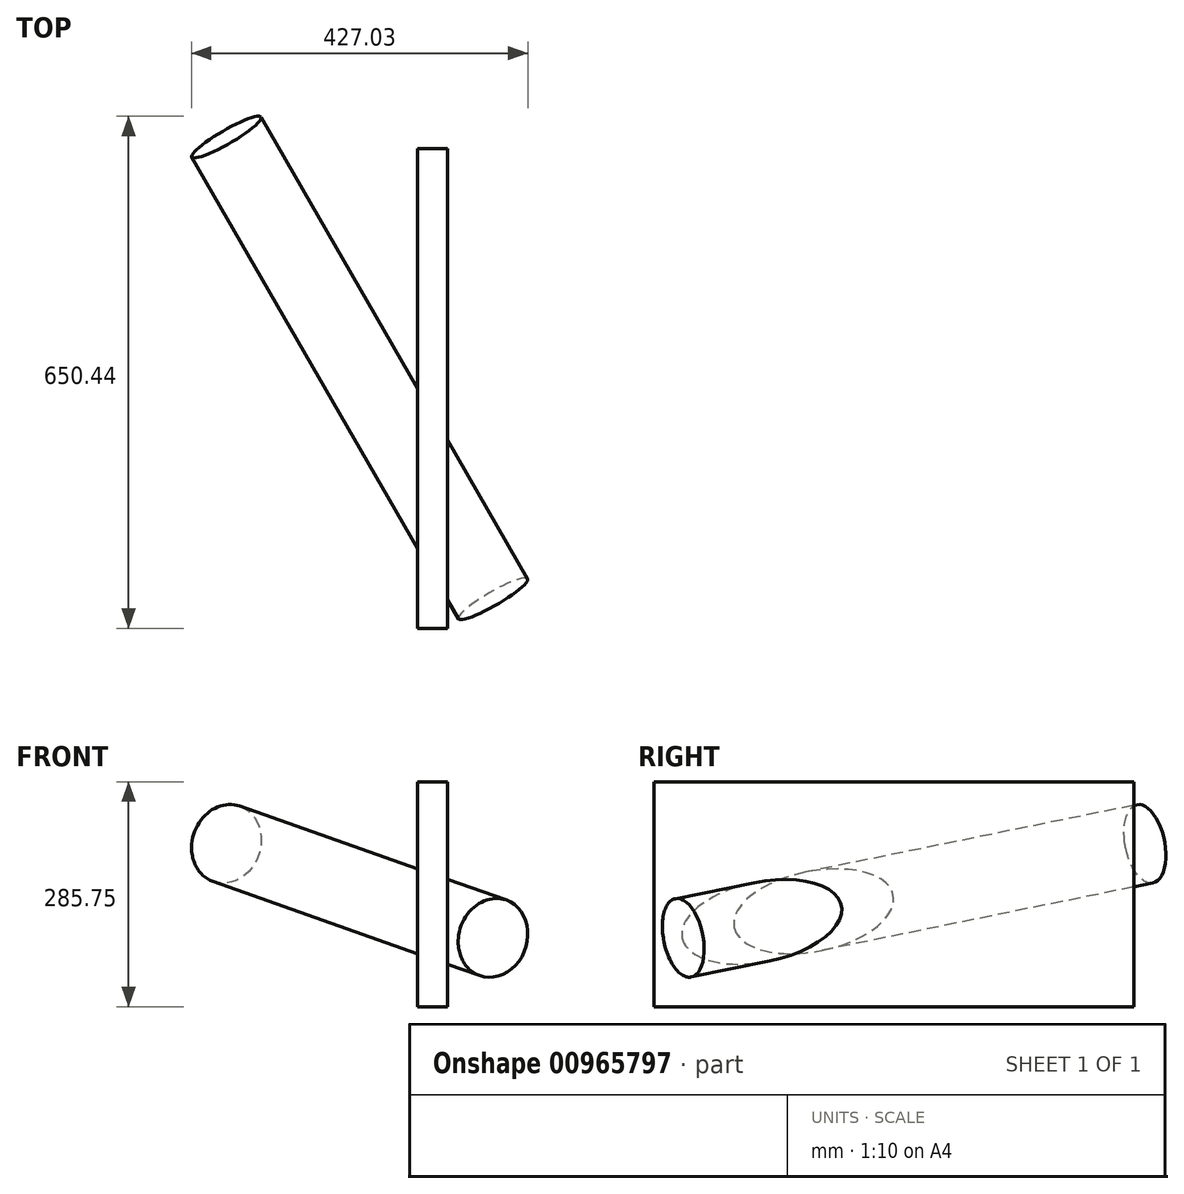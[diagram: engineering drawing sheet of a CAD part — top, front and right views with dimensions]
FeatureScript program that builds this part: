
annotation { "Feature Type Name" : "Feature", "Feature Type Description" : "" }
export const myFeature = defineFeature(function(context is Context, id is Id, definition is map)
    precondition{}
    {
        {
            var Q0;
            Q0=qCreatedBy(makeId("Front.planeOp"),FACE);
            var sketch = newSketch(context, id + "F0", { "sketchPlane" : qUnion([Q0])});
            skLineSegment(sketch, "E0.bottom", {"start": v(0, 0) * mm, "end": v(38.1, 0) * mm});
            skLineSegment(sketch, "E0.top", {"start": v(0, 285.75) * mm, "end": v(38.1, 285.75) * mm});
            skLineSegment(sketch, "E0.left", {"start": v(0, 0) * mm, "end": v(0, 285.75) * mm});
            skLineSegment(sketch, "E0.right", {"start": v(38.1, 0) * mm, "end": v(38.1, 285.75) * mm});
            skSolve(sketch);
        }
        {
            var Q0;
            Q0 = qSketchRegion(id + "F0", true);
            extrude(context, id + "F1", {"entities" : qUnion([Q0]), "oppositeDirection" : true, "depth" : 609.6 * mm, "offsetDistance" : 25.4 * mm});
        }
        {
            var Q0;
            Q0=makeQuery(id+"F1.opExtrude","CAP_EDGE",EDGE,{"disambiguationData":[OSD([sQuery(id+"F0.wireOp",EDGE,"E0.left")])],"isStart":true});
            cPlane(context, id + "F2", {"entities" : qUnion([Q0]), "cplaneType" : CPlaneType.LINE_ANGLE, "offset" : 25.4 * mm, "angle" : 60 * degree, "oppositeDirection" : true, "width" : 152.4 * mm, "height" : 152.4 * mm});
        }
        {
            var Q0;
            Q0=qCreatedBy(id+"F2.planeOp",FACE);
            var sketch = newSketch(context, id + "F3", { "sketchPlane" : qUnion([Q0])});
            skLineSegment(sketch, "E1", {"start": v(0, 0) * mm, "end": v(122.92, 0) * mm});
            skSolve(sketch);
        }
        {
            var Q0;
            Q0=sQuery(id+"F3.wireOp",EDGE,"E1");
            cPlane(context, id + "F4", {"entities" : qUnion([Q0]), "cplaneType" : CPlaneType.LINE_ANGLE, "offset" : 25.4 * mm, "angle" : 10 * degree, "width" : 152.4 * mm, "height" : 152.4 * mm});
        }
        {
            var Q0;
            Q0=qCreatedBy(id+"F4.planeOp",FACE);
            var sketch = newSketch(context, id + "F5", { "sketchPlane" : qUnion([Q0])});
            skCircle(sketch, "E2", {"center": v(-109.95, 78.2) * mm, "radius": 50.8 * mm});
            skLineSegment(sketch, "E3", {"start": v(-109.95, 208.3) * mm, "end": v(-109.95, -138.84) * mm, "construction": true});
            skLineSegment(sketch, "E4", {"start": v(-284.16, 78.2) * mm, "end": v(134.51, 78.2) * mm, "construction": true});
            skPoint(sketch, "E5", {"position": v(-160.75, 78.2) * mm});
            skPoint(sketch, "E6", {"position": v(-109.95, 27.4) * mm});
            skPoint(sketch, "E7", {"position": v(-109.95, 129) * mm});
            skPoint(sketch, "E8", {"position": v(-59.15, 78.2) * mm});
            skSolve(sketch);
        }
        {
            var Q0;
            Q0 = qSketchRegion(id + "F5", true);
            extrude(context, id + "F6", {"entities" : qUnion([Q0]), "operationType" : NewBodyOperationType.ADD, "endBound" : BoundingType.THROUGH_ALL, "depth" : 25.4 * mm, "offsetDistance" : 25.4 * mm});
        }
    });
